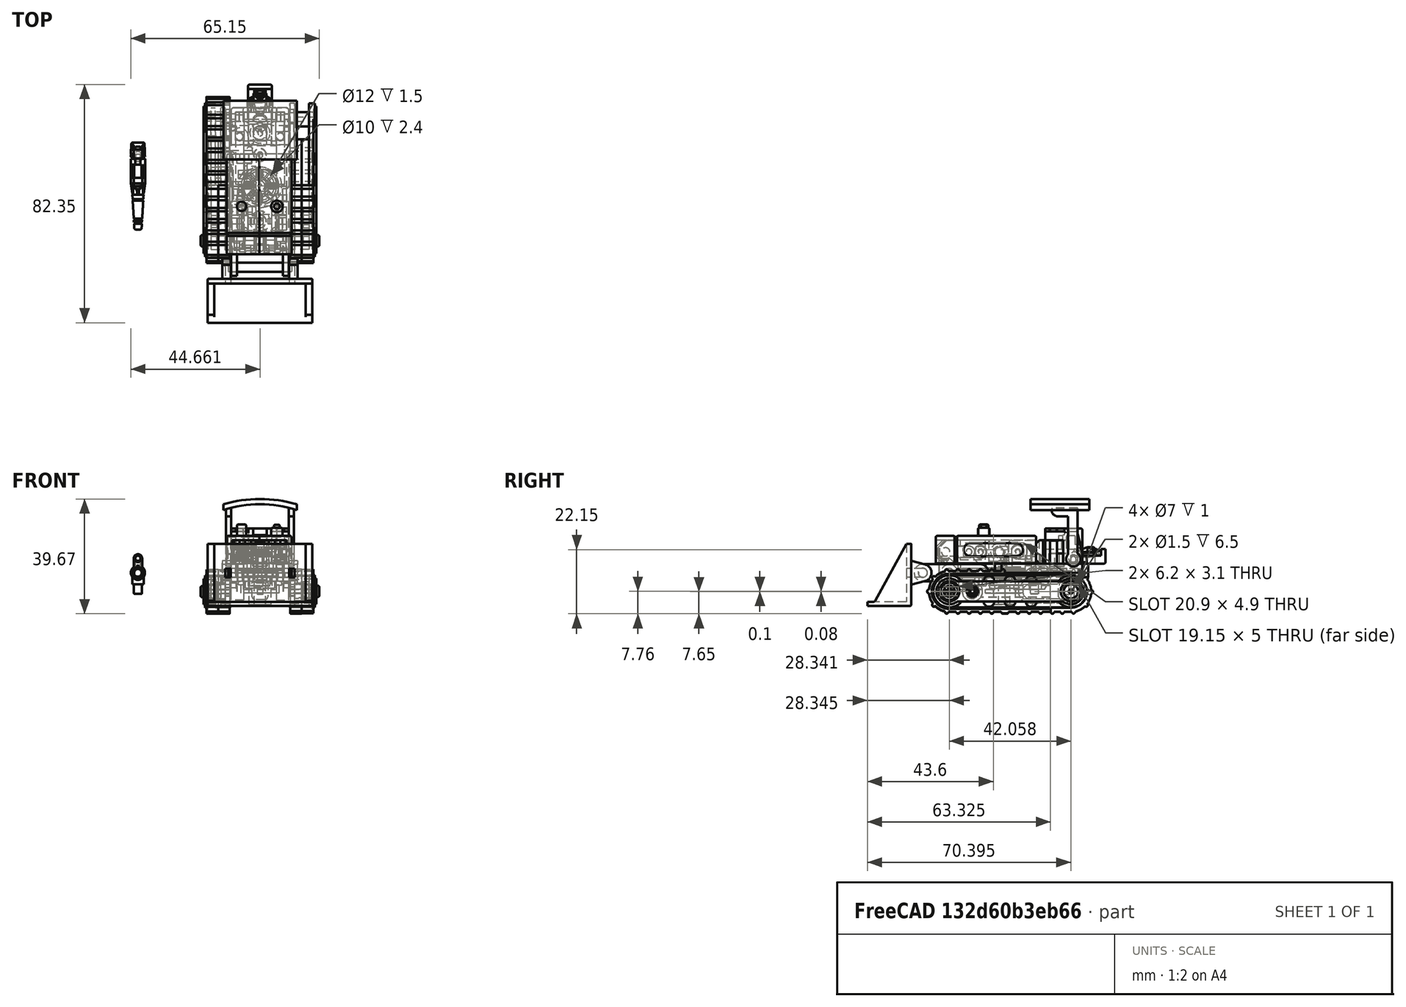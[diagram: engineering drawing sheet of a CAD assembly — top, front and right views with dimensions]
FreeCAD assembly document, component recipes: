
FREECAD ASSEMBLY — COMPONENT RECIPES ("Bonecrusher")

This assembly document has 22 components, labeled P0..P21 below (a component is one placed body or linked part). 22 of them carry a construction recipe — the FreeCAD feature program that regenerates the part from scratch, quoted from this document or its linked companion documents; the rest are supplied as boundary geometry only. No exploded tour is included for this assembly.
NOTE — document 4 of 4 of this assembly tour. The two overview renders and the header above are repeated from document 1; the component sections below continue where the previous document stopped.
COMPONENT P21 — recipe-attached ("Head", modeled in this document).
Construction recipe (the document's own serialized feature program — sketch geometry with constraints, then the solid features built on it; lengths are millimeters unless a unit is written):

FEATURE [Sketcher::SketchObject] Sketch142
  ArcFitTolerance = 1e-06
  AttachmentSupport = -> [XY_Plane015]
  FullyConstrained = true
  MakeInternals = false
  MapMode = 5
  sketch-geometry (4):
    g0: LineSegment StartX=0 StartY=0 StartZ=0 EndX=8.1 EndY=0 EndZ=0
    g1: LineSegment StartX=8.1 StartY=0 StartZ=0 EndX=8.1 EndY=12 EndZ=0
    g2: LineSegment StartX=8.1 StartY=12 StartZ=0 EndX=0 EndY=12 EndZ=0
    g3: LineSegment StartX=0 StartY=12 StartZ=0 EndX=0 EndY=0 EndZ=0
  constraints (11):
    c: Coincident(g0,g1)
    c: Coincident(g1,g2)
    c: Coincident(g2,g3)
    c: Coincident(g3,g0)
    c: Horizontal(g0)
    c: Horizontal(g2)
    c: Vertical(g1)
    c: Vertical(g3)
    c: Coincident(g0,g-1)
    c: DistanceX(g0,g0) = 8.1
    c: DistanceY(g3,g3) = 12
FEATURE [PartDesign::Pad] Pad073
  Direction = (0,0,1)
  Length = 2.8
  Length2 = 10
  Profile = -> Sketch142
  ReferenceAxis = -> Sketch142 [N_Axis]
  Refine = true
  Suppressed = false
  Type = 0
FEATURE [Sketcher::SketchObject] Sketch143
  ArcFitTolerance = 1e-06
  AttachmentSupport = -> [Pad073]
  ExternalGeometry = -> [Pad073]
  FullyConstrained = true
  MakeInternals = false
  MapMode = 5
  Placement = pos=(0,0,2.8) rot=(0,0,1;0rad)
  sketch-geometry (4):
    g0: LineSegment StartX=0 StartY=12 StartZ=0 EndX=0 EndY=10.5 EndZ=0
    g1: LineSegment StartX=0 StartY=10.5 StartZ=0 EndX=8.1 EndY=10.5 EndZ=0
    g2: LineSegment StartX=8.1 StartY=10.5 StartZ=0 EndX=8.1 EndY=12 EndZ=0
    g3: LineSegment StartX=8.1 StartY=12 StartZ=0 EndX=0 EndY=12 EndZ=0
  constraints (11):
    c: Coincident(g0,g1)
    c: Coincident(g1,g2)
    c: Coincident(g2,g3)
    c: Coincident(g3,g0)
    c: Vertical(g0)
    c: Vertical(g2)
    c: Horizontal(g1)
    c: Horizontal(g3)
    c: Coincident(g0,g-4)
    c: PointOnObject(g1,g-3)
    c: DistanceY(g0,g0) = 1.5
FEATURE [PartDesign::Pad] Pad074
  BaseFeature = -> Pad073
  Direction = (0,0,1)
  Length = 2.25
  Length2 = 10
  Profile = -> Sketch143
  ReferenceAxis = -> Sketch143 [N_Axis]
  Refine = true
  Suppressed = false
  Type = 0
FEATURE [Sketcher::SketchObject] Sketch144
  ArcFitTolerance = 1e-06
  AttachmentSupport = -> [Pad074]
  FullyConstrained = true
  MakeInternals = false
  MapMode = 5
  Placement = pos=(0,0,0) rot=(0.57735,-0.57735,-0.57735;2.0944rad)
  sketch-geometry (2):
    g0: ArcOfCircle CenterX=-1.25 CenterY=2.8 CenterZ=0 NormalX=0 NormalY=0 NormalZ=1 AngleXU=0 Radius=1.25 StartAngle=0 EndAngle=3.14159
    g1: LineSegment StartX=-2.5 StartY=2.8 StartZ=0 EndX=-1.29e-14 EndY=2.8 EndZ=0
  constraints (6):
    c: Coincident(g0,g-3)
    c: PointOnObject(g0,g-3)
    c: Diameter(g0) = 2.5
    c: PointOnObject(g0,g-3)
    c: Coincident(g1,g0)
    c: Coincident(g1,g0)
FEATURE [PartDesign::Pad] Pad075
  BaseFeature = -> Pad074
  Direction = (-1,0,0)
  Length = 10
  Length2 = 10
  Profile = -> Sketch144
  ReferenceAxis = -> Sketch144 [N_Axis]
  Refine = true
  Suppressed = false
  Type = 0
FEATURE [Sketcher::SketchObject] Sketch145
  ArcFitTolerance = 1e-06
  AttachmentSupport = -> [Pad075]
  ExternalGeometry = -> [Pad075]
  FullyConstrained = true
  MakeInternals = false
  MapMode = 5
  Placement = pos=(0,0,0) rot=(0.57735,-0.57735,-0.57735;2.0944rad)
  sketch-geometry (2):
    g0: ArcOfCircle CenterX=-1.25 CenterY=2.79999 CenterZ=0 NormalX=0 NormalY=0 NormalZ=1 AngleXU=0 Radius=1.25 StartAngle=7.57041e-06 EndAngle=3.14159
    g1: LineSegment StartX=-2.5 StartY=2.8 StartZ=0 EndX=-3.58256e-11 EndY=2.8 EndZ=0
  constraints (5):
    c: Coincident(g0,g-3)
    c: Coincident(g0,g-3)
    c: Diameter(g0) = 2.5
    c: Coincident(g1,g0)
    c: Coincident(g1,g0)
FEATURE [PartDesign::Pad] Pad076
  BaseFeature = -> Pad075
  Direction = (-1,0,0)
  Length = 9.6
  Length2 = 10
  Profile = -> Sketch145
  ReferenceAxis = -> Sketch145 [N_Axis]
  Refine = true
  Reversed = true
  Suppressed = false
  Type = 0
FEATURE [PartDesign::Pad] Pad077
  BaseFeature = -> Pad076
  Direction = (-1,0,0)
  Length = 1.5
  Length2 = 10
  Profile = -> Sketch145
  ReferenceAxis = -> Sketch145 [N_Axis]
  Refine = true
  Suppressed = false
  Type = 0
FEATURE [Sketcher::SketchObject] Sketch313
  ArcFitTolerance = 1e-06
  AttachmentSupport = -> [Pad077]
  ExternalGeometry = -> [Pad077]
  FullyConstrained = true
  MakeInternals = false
  MapMode = 5
  Placement = pos=(0,0,0) rot=(1,0,0;3.14159rad)
  sketch-geometry (1):
    g0: Circle CenterX=4.05 CenterY=-6 CenterZ=0 NormalX=0 NormalY=0 NormalZ=1 AngleXU=0 Radius=2.35
  constraints (5):
    c: Diameter(g0) = 4.7
    c: DistanceX(g-3,g-3) = 8.1
    c: DistanceY(g-4,g-4) = 12
    c: DistanceY(g0,g-1) = 6
    c: DistanceX(g-1,g0) = 4.05
FEATURE [PartDesign::Pocket] Pocket150
  BaseFeature = -> Pad077
  Direction = (0,0,1)
  Length = 2.2
  Length2 = 5
  Profile = -> Sketch313
  ReferenceAxis = -> Sketch313 [N_Axis]
  Refine = true
  Suppressed = false
  Type = 0
FEATURE [PartDesign::Pad] Pad179
  BaseFeature = -> Pocket150
  Direction = (-1,0,0)
  Length = 0.05
  Length2 = 10
  Profile = -> Pocket150 [Face2]
  Refine = true
  Suppressed = false
  Type = 0
FEATURE [PartDesign::Pad] Pad180
  BaseFeature = -> Pad179
  Direction = (1,0,0)
  Length = 0.05
  Length2 = 10
  Profile = -> Pad179 [Face3]
  Refine = true
  Suppressed = false
  Type = 0
FEATURE [PartDesign::Fillet] Fillet050
  Base = -> Pad180 [Edge7,Edge1,Edge26,Edge21,Edge20]
  BaseFeature = -> Pad180
  Radius = 0.5
  Refine = true
  SupportTransform = false
  Suppressed = false
  UseAllEdges = false
FEATURE [Sketcher::SketchObject] Sketch314
  ArcFitTolerance = 1e-06
  AttachmentOffset = pos=(0,0,-1.9) rot=(0,0,1;0rad)
  AttachmentSupport = -> [Fillet050]
  ExternalGeometry = -> [Fillet050]
  FullyConstrained = true
  MakeInternals = false
  MapMode = 5
  Placement = pos=(1.85,0,0) rot=(0.57735,-0.57735,-0.57735;2.0944rad)
  sketch-geometry (3):
    g0: LineSegment StartX=-5.8 StartY=2.8 StartZ=0 EndX=-9 EndY=2.8 EndZ=0
    g1: LineSegment StartX=-5.8 StartY=2.8 StartZ=0 EndX=-5.8 EndY=5.8 EndZ=0
    g2: ArcOfCircle CenterX=-3.95033 CenterY=0.620354 CenterZ=0 NormalX=0 NormalY=0 NormalZ=1 AngleXU=0 Radius=5.5 StartAngle=1.91379 EndAngle=2.73411
  constraints (10):
    c: PointOnObject(g0,g-3)
    c: PointOnObject(g0,g-3)
    c: DistanceX(g0,g0) = 3.2
    c: DistanceX(g-3,g0) = 1.5
    c: Coincident(g1,g0)
    c: Vertical(g1)
    c: DistanceY(g1,g1) = 3
    c: Coincident(g2,g1)
    c: Coincident(g2,g0)
    c: Radius(g2) = 5.5
FEATURE [PartDesign::Pad] Pad181
  BaseFeature = -> Fillet050
  Direction = (-1,0,0)
  Length = 4.4
  Length2 = 10
  Profile = -> Sketch314
  ReferenceAxis = -> Sketch314 [N_Axis]
  Refine = true
  Reversed = true
  Suppressed = false
  Type = 0
FEATURE [Sketcher::SketchObject] Sketch315
  ArcFitTolerance = 1e-06
  AttachmentSupport = -> [Pad181]
  ExternalGeometry = -> [Pad181]
  FullyConstrained = true
  MakeInternals = false
  MapMode = 5
  Placement = pos=(0,0,2.8) rot=(0,0,1;0rad)
  sketch-geometry (4):
    g0: LineSegment StartX=1.85 StartY=5.8 StartZ=0 EndX=2.7 EndY=2.5 EndZ=0
    g1: LineSegment StartX=6.25 StartY=5.8 StartZ=0 EndX=5.4 EndY=2.5 EndZ=0
    g2: LineSegment StartX=5.4 StartY=2.5 StartZ=0 EndX=2.7 EndY=2.5 EndZ=0
    g3: LineSegment StartX=1.85 StartY=5.8 StartZ=0 EndX=6.25 EndY=5.8 EndZ=0
  constraints (11):
    c: Coincident(g0,g-4)
    c: PointOnObject(g0,g-3)
    c: Coincident(g1,g-4)
    c: PointOnObject(g1,g-3)
    c: Coincident(g2,g1)
    c: Coincident(g2,g0)
    c: DistanceX(g2,g2) = 2.7
    c: DistanceX(g-4,g-4) = 4.4
    c: DistanceX(g0,g0) = 0.85
    c: Coincident(g3,g0)
    c: Coincident(g3,g1)
FEATURE [PartDesign::Pad] Pad182
  BaseFeature = -> Pad181
  Direction = (0,0,1)
  Length = 0.5
  Length2 = 10
  Profile = -> Sketch315
  ReferenceAxis = -> Sketch315 [N_Axis]
  Refine = true
  Suppressed = false
  Type = 0
FEATURE [Sketcher::SketchObject] Sketch316
  ArcFitTolerance = 1e-06
  AttachmentSupport = -> [Pad182]
  ExternalGeometry = -> [Pad182]
  FullyConstrained = true
  MakeInternals = false
  MapMode = 5
  Placement = pos=(0,0,2.8) rot=(0,0,1;0rad)
  sketch-geometry (14):
    g0: LineSegment StartX=2.7 StartY=2.5 StartZ=0 EndX=1.85 EndY=2.5 EndZ=0
    g1: LineSegment StartX=2.7 StartY=2.5 StartZ=0 EndX=1.85 EndY=5.8 EndZ=0
    g2: LineSegment StartX=1.85 StartY=5.8 StartZ=0 EndX=1.55 EndY=5.8 EndZ=0
    g3: LineSegment StartX=1.55 StartY=5.8 StartZ=0 EndX=1.5628 EndY=3.90004 EndZ=0
    g4: LineSegment StartX=1.5628 StartY=3.90004 StartZ=0 EndX=1.85 EndY=3.7 EndZ=0
    g5: LineSegment StartX=1.85 StartY=3.7 StartZ=0 EndX=1.85 EndY=2.5 EndZ=0
    g6: LineSegment StartX=5.4 StartY=2.5 StartZ=0 EndX=6.25 EndY=2.5 EndZ=0
    g7: LineSegment StartX=6.25 StartY=2.5 StartZ=0 EndX=6.25 EndY=3.7 EndZ=0
    g8: LineSegment StartX=6.25 StartY=3.7 StartZ=0 EndX=6.5628 EndY=3.90004 EndZ=0
    g9: LineSegment StartX=6.5628 StartY=3.90004 StartZ=0 EndX=6.55 EndY=5.8 EndZ=0
    g10: LineSegment StartX=6.55 StartY=5.8 StartZ=0 EndX=6.25 EndY=5.8 EndZ=0
    g11: LineSegment StartX=6.25 StartY=5.8 StartZ=0 EndX=5.4 EndY=2.5 EndZ=0
    g12: LineSegment [constr] StartX=1.85 StartY=3.7 StartZ=0 EndX=6.25 EndY=3.7 EndZ=0
    g13: LineSegment [constr] StartX=1.5628 StartY=3.90004 StartZ=0 EndX=6.5628 EndY=3.90004 EndZ=0
  constraints (36):
    c: Coincident(g0,g-4)
    c: Coincident(g1,g0)
    c: Coincident(g1,g-3)
    c: Coincident(g2,g1)
    c: Horizontal(g2)
    c: Coincident(g3,g2)
    c: Coincident(g4,g3)
    c: Coincident(g5,g4)
    c: Coincident(g5,g0)
    c: Vertical(g5)
    c: DistanceY(g5,g5) = 1.2
    c: DistanceX(g-4,g0) = 1.9
    c: DistanceX(g2,g2) = 0.3
    c: PointOnObject(g0,g-4)
    c: Distance(g3) = 1.9
    c: Distance(g4) = 0.35
    c: Coincident(g6,g-6)
    c: PointOnObject(g6,g-6)
    c: Coincident(g7,g6)
    c: Vertical(g7)
    c: Coincident(g8,g7)
    c: Coincident(g9,g8)
    c: Coincident(g10,g9)
    c: Coincident(g10,g-5)
    c: Coincident(g11,g10)
    c: Coincident(g11,g6)
    c: DistanceX(g10,g10) = 0.3
    c: Horizontal(g10)
    c: DistanceX(g6,g-7) = 1.9
    c: Coincident(g12,g4)
    c: Coincident(g12,g7)
    c: Horizontal(g12)
    c: Coincident(g13,g3)
    c: Coincident(g13,g8)
    c: Horizontal(g13)
    c: Distance(g9) = 1.9
FEATURE [PartDesign::Pad] Pad183
  BaseFeature = -> Pad182
  Direction = (0,0,1)
  Length = 0.5
  Length2 = 10
  Profile = -> Sketch316
  ReferenceAxis = -> Sketch316 [N_Axis]
  Refine = true
  Suppressed = false
  Type = 0
FEATURE [Sketcher::SketchObject] Sketch317
  ArcFitTolerance = 1e-06
  AttachmentSupport = -> [Pad183]
  ExternalGeometry = -> [Pad183]
  FullyConstrained = true
  MakeInternals = false
  MapMode = 5
  Placement = pos=(0,0,2.8) rot=(0,0,1;0rad)
  sketch-geometry (20):
    g0: LineSegment StartX=6.5628 StartY=3.90004 StartZ=0 EndX=7.51163 EndY=4.50684 EndZ=0
    g1: LineSegment StartX=7.65 StartY=4.75957 StartZ=0 EndX=7.65 EndY=6.932 EndZ=0
    g2: LineSegment StartX=7.51282 StartY=7.18397 StartZ=0 EndX=6.25 EndY=8 EndZ=0
    g3: LineSegment StartX=6.25 StartY=8 StartZ=0 EndX=6.25 EndY=5.8 EndZ=0
    g4: LineSegment StartX=6.25 StartY=5.8 StartZ=0 EndX=6.55 EndY=5.8 EndZ=0
    g5: LineSegment StartX=6.55 StartY=5.8 StartZ=0 EndX=6.5628 EndY=3.90004 EndZ=0
    g6: ArcOfCircle CenterX=7.35 CenterY=4.75957 CenterZ=0 NormalX=0 NormalY=0 NormalZ=1 AngleXU=0 Radius=0.3 StartAngle=5.28136 EndAngle=6.28319
    g7: GeomPoint [constr] X=7.65 Y=4.59533 Z=0
    g8: ArcOfCircle CenterX=7.35 CenterY=6.932 CenterZ=0 NormalX=0 NormalY=0 NormalZ=1 AngleXU=0 Radius=0.3 StartAngle=1e-16 EndAngle=0.997101
    g9: GeomPoint [constr] X=7.65 Y=7.09533 Z=0
    g10: LineSegment StartX=1.5628 StartY=3.90004 StartZ=0 EndX=1.55 EndY=5.8 EndZ=0
    g11: LineSegment StartX=1.55 StartY=5.8 StartZ=0 EndX=1.85 EndY=5.8 EndZ=0
    g12: LineSegment StartX=1.85 StartY=5.8 StartZ=0 EndX=1.85 EndY=8 EndZ=0
    g13: LineSegment StartX=1.85 StartY=8 StartZ=0 EndX=0.597712 EndY=7.26218 EndZ=0
    g14: LineSegment StartX=1.5628 StartY=3.90004 StartZ=0 EndX=0.578534 EndY=4.58562 EndZ=0
    g15: LineSegment StartX=0.45 StartY=7.0037 StartZ=0 EndX=0.45 EndY=4.83179 EndZ=0
    g16: ArcOfCircle CenterX=0.75 CenterY=7.0037 CenterZ=0 NormalX=0 NormalY=0 NormalZ=1 AngleXU=0 Radius=0.3 StartAngle=2.10322 EndAngle=3.14159
    g17: GeomPoint [constr] X=0.45 Y=7.17515 Z=0
    g18: ArcOfCircle CenterX=0.75 CenterY=4.83179 CenterZ=0 NormalX=0 NormalY=0 NormalZ=1 AngleXU=0 Radius=0.3 StartAngle=3.14159 EndAngle=4.10399
    g19: GeomPoint [constr] X=0.45 Y=4.67515 Z=0
  constraints (46):
    c: Coincident(g0,g-3)
    c: Vertical(g1)
    c: PointOnObject(g2,g-4)
    c: Coincident(g3,g2)
    c: Coincident(g3,g-4)
    c: Coincident(g4,g3)
    c: Coincident(g4,g-3)
    c: Coincident(g5,g4)
    c: Coincident(g5,g0)
    c: DistanceX(g9,g-5) = 0.5
    c: Parallel(g-7,g0)
    c: DistanceY(g7,g9) = 2.5
    c: DistanceY(g3,g3) = 2.2
    c: PointOnObject(g7,g0)
    c: PointOnObject(g7,g1)
    c: Tangent(g0,g6) = -1.5708
    c: Tangent(g1,g6) = -1.5708
    c: PointOnObject(g9,g1)
    c: PointOnObject(g9,g2)
    c: Tangent(g1,g8) = -1.5708
    c: Tangent(g2,g8) = -1.5708
    c: Radius(g8) = 0.3
    c: Radius(g6) = 0.3
    c: Coincident(g10,g-9)
    c: Coincident(g10,g-10)
    c: Coincident(g11,g-9)
    c: Coincident(g11,g-11)
    c: Coincident(g12,g11)
    c: PointOnObject(g12,g-11)
    c: Coincident(g13,g12)
    c: Coincident(g14,g10)
    c: Vertical(g15)
    c: PointOnObject(g17,g13)
    c: PointOnObject(g17,g15)
    c: Tangent(g13,g16) = -1.5708
    c: Tangent(g15,g16) = -1.5708
    c: PointOnObject(g19,g14)
    c: PointOnObject(g19,g15)
    c: Tangent(g14,g18) = 1.5708
    c: Tangent(g15,g18) = -1.5708
    c: Radius(g18) = 0.3
    c: Radius(g16) = 0.3
    c: DistanceX(g-6,g15) = 0.5
    c: DistanceY(g19,g17) = 2.5
    c: DistanceY(g11,g12) = 2.2
    c: Parallel(g-8,g14)
FEATURE [PartDesign::Pad] Pad184
  BaseFeature = -> Pad183
  Direction = (0,0,1)
  Length = 1.2
  Length2 = 10
  Profile = -> Sketch317
  ReferenceAxis = -> Sketch317 [N_Axis]
  Refine = true
  Suppressed = false
  Type = 0
FEATURE [PartDesign::Chamfer] Chamfer003
  Angle = 45
  Base = -> Pad184 [Edge109,Edge61,Edge63,Edge67,Edge65,Edge113,Edge77,Edge79,Edge81,Edge83]
  BaseFeature = -> Pad184
  ChamferType = 0
  FlipDirection = false
  Refine = true
  Size = 0.299
  Size2 = 1
  SupportTransform = false
  Suppressed = false
  UseAllEdges = false
FEATURE [Sketcher::SketchObject] Sketch318
  ArcFitTolerance = 1e-06
  AttachmentSupport = -> [Chamfer003]
  ExternalGeometry = -> [Chamfer003]
  FullyConstrained = true
  MakeInternals = false
  MapMode = 5
  Placement = pos=(0,0,3.3) rot=(0,0,1;0rad)
  sketch-geometry (6):
    g0: LineSegment [constr] StartX=2.7 StartY=2.5 StartZ=0 EndX=1.85 EndY=5.8 EndZ=0
    g1: LineSegment [constr] StartX=5.4 StartY=2.5 StartZ=0 EndX=6.25 EndY=5.8 EndZ=0
    g2: LineSegment StartX=5.91515 StartY=4.5 StartZ=0 EndX=2.18485 EndY=4.5 EndZ=0
    g3: LineSegment StartX=2.18485 StartY=4.5 StartZ=0 EndX=3.02197 EndY=1.25 EndZ=0
    g4: LineSegment StartX=5.91515 StartY=4.5 StartZ=0 EndX=5.07803 EndY=1.25 EndZ=0
    g5: LineSegment StartX=5.07803 StartY=1.25 StartZ=0 EndX=3.02197 EndY=1.25 EndZ=0
  constraints (17):
    c: Coincident(g0,g-3)
    c: Coincident(g0,g-4)
    c: Coincident(g1,g-3)
    c: Coincident(g1,g-4)
    c: PointOnObject(g2,g1)
    c: PointOnObject(g2,g0)
    c: Horizontal(g2)
    c: DistanceY(g0,g2) = 2
    c: Coincident(g3,g2)
    c: Coincident(g4,g2)
    c: Coincident(g5,g4)
    c: Coincident(g5,g3)
    c: Horizontal(g5)
    c: PointOnObject(g0,g3)
    c: PointOnObject(g1,g4)
    c: DistanceY(g-5,g-5) = 2.5
    c: DistanceY(g3,g-5) = 1.25
FEATURE [PartDesign::Pad] Pad185
  BaseFeature = -> Chamfer003
  Direction = (0,0,1)
  Length = 2
  Length2 = 10
  Profile = -> Sketch318
  ReferenceAxis = -> Sketch318 [N_Axis]
  Refine = true
  Suppressed = false
  Type = 0
FEATURE [Sketcher::SketchObject] Sketch319
  ArcFitTolerance = 1e-06
  AttachmentSupport = -> [Pad185]
  ExternalGeometry = -> [Pad185]
  FullyConstrained = true
  MakeInternals = false
  MapMode = 5
  Placement = pos=(1.85,0,0) rot=(0.57735,-0.57735,-0.57735;2.0944rad)
  sketch-geometry (5):
    g0: LineSegment [constr] StartX=-5.8 StartY=5.8 StartZ=0 EndX=-1.25 EndY=4.04999 EndZ=0
    g1: LineSegment StartX=-5.8 StartY=5.8 StartZ=0 EndX=-1.25 EndY=4.04999 EndZ=0
    g2: LineSegment StartX=-1.25 StartY=4.04999 StartZ=0 EndX=-1.25 EndY=5.8 EndZ=0
    g3: LineSegment StartX=-1.25 StartY=5.8 StartZ=0 EndX=-5.8 EndY=5.8 EndZ=0
    g4: LineSegment [constr] StartX=-1.25 StartY=4.04999 StartZ=0 EndX=-1.25 EndY=2.79999 EndZ=0
  constraints (12):
    c: Coincident(g0,g-4)
    c: PointOnObject(g0,g-3)
    c: Coincident(g1,g0)
    c: Coincident(g1,g0)
    c: Coincident(g2,g0)
    c: Coincident(g3,g2)
    c: Coincident(g3,g0)
    c: Horizontal(g3)
    c: Vertical(g2)
    c: Coincident(g4,g0)
    c: Coincident(g4,g-3)
    c: Vertical(g4)
FEATURE [PartDesign::Pocket] Pocket151
  BaseFeature = -> Pad185
  Direction = (1,0,0)
  Length = 5
  Length2 = 5
  Profile = -> Sketch319
  ReferenceAxis = -> Sketch319 [N_Axis]
  Refine = true
  Suppressed = false
  Type = 0
FEATURE [PartDesign::Pad] Pad186
  BaseFeature = -> Pocket151
  Direction = (0,0,1)
  Length = 1
  Length2 = 10
  Profile = -> Sketch318
  ReferenceAxis = -> Sketch318 [N_Axis]
  Refine = true
  Reversed = true
  Suppressed = false
  Type = 0
FEATURE [Sketcher::SketchObject] Sketch320
  ArcFitTolerance = 1e-06
  AttachmentSupport = -> [Pad186]
  ExternalGeometry = -> [Pad186]
  FullyConstrained = true
  MakeInternals = false
  MapMode = 5
  Placement = pos=(1.85,0,0) rot=(0.57735,-0.57735,-0.57735;2.0944rad)
  sketch-geometry (4):
    g0: LineSegment StartX=-3.9 StartY=3.3 StartZ=0 EndX=-2.83669 EndY=4.66026 EndZ=0
    g1: LineSegment StartX=-2.83669 StartY=4.66026 StartZ=0 EndX=-4.5 EndY=5.3 EndZ=0
    g2: LineSegment StartX=-4.5 StartY=5.3 StartZ=0 EndX=-4.5 EndY=3.3 EndZ=0
    g3: LineSegment StartX=-4.5 StartY=3.3 StartZ=0 EndX=-3.9 EndY=3.3 EndZ=0
  constraints (10):
    c: PointOnObject(g0,g-7)
    c: PointOnObject(g0,g-3)
    c: Coincident(g1,g0)
    c: Coincident(g1,g-4)
    c: Coincident(g2,g1)
    c: Coincident(g2,g-7)
    c: Coincident(g3,g2)
    c: Coincident(g3,g0)
    c: Distance(g0,g-3) = 1.7
    c: Distance(g-7,g0) = 1.4
FEATURE [PartDesign::Pocket] Pocket152
  BaseFeature = -> Pad186
  Direction = (1,0,0)
  Length = 5
  Length2 = 5
  Profile = -> Sketch320
  ReferenceAxis = -> Sketch320 [N_Axis]
  Refine = true
  Suppressed = false
  Type = 0
FEATURE [PartDesign::SubShapeBinder] Binder
  BindCopyOnChange = 0
  BindMode = 2
  ClaimChildren = false
  Context = -> Part [Body025.Binder.]
  Fuse = false
  MakeFace = true
  OffsetFill = false
  OffsetIntersection = false
  OffsetJoinType = 0
  OffsetOpenResult = false
  PartialLoad = false
  Refine = true
  Relative = true
  _Version = 2
FEATURE [Sketcher::SketchObject] Sketch321
  ArcFitTolerance = 1e-06
  AttachmentSupport = -> [Binder]
  ExternalGeometry = -> [Binder]
  FullyConstrained = true
  MakeInternals = false
  MapMode = 5
  Placement = pos=(0,0,6.5) rot=(0,0,1;0rad)
  sketch-geometry (6):
    g0: LineSegment StartX=36.1 StartY=-3.2 StartZ=0 EndX=36.85 EndY=-6.15 EndZ=0
    g1: LineSegment StartX=36.85 StartY=-6.15 StartZ=0 EndX=39.55 EndY=-6.15 EndZ=0
    g2: LineSegment StartX=39.55 StartY=-6.15 StartZ=0 EndX=40.3 EndY=-3.2 EndZ=0
    g3: LineSegment StartX=40.3 StartY=-3.2 StartZ=0 EndX=36.1 EndY=-3.2 EndZ=0
    g4: LineSegment [constr] StartX=39.55 StartY=-6.15 StartZ=0 EndX=39.55 EndY=-6.5 EndZ=0
    g5: LineSegment [constr] StartX=36.85 StartY=-6.15 StartZ=0 EndX=36.85 EndY=-6.5 EndZ=0
  constraints (16):
    c: PointOnObject(g0,g-3)
    c: Coincident(g1,g0)
    c: Horizontal(g1)
    c: Coincident(g2,g1)
    c: PointOnObject(g2,g-3)
    c: Coincident(g3,g2)
    c: Coincident(g3,g0)
    c: DistanceX(g-7,g0) = 0.4
    c: DistanceX(g2,g-6) = 0.4
    c: Coincident(g4,g1)
    c: Coincident(g4,g-5)
    c: Vertical(g4)
    c: Coincident(g5,g0)
    c: Coincident(g5,g-8)
    c: Vertical(g5)
    c: DistanceY(g5,g0) = 0.35
FEATURE [PartDesign::Pad] Pad187
  Direction = (0,0,1)
  Length = 2.4
  Length2 = 10
  Profile = -> Sketch321
  ReferenceAxis = -> Sketch321 [N_Axis]
  Refine = true
  Suppressed = false
  Type = 0
FEATURE [PartDesign::SubShapeBinder] Binder002
  BindCopyOnChange = 0
  BindMode = 2
  ClaimChildren = false
  Context = -> Part [Body025.Binder002.]
  Fuse = false
  MakeFace = true
  OffsetFill = false
  OffsetIntersection = false
  OffsetJoinType = 0
  OffsetOpenResult = false
  PartialLoad = false
  Refine = true
  Relative = true
  _Version = 2
FEATURE [Sketcher::SketchObject] Sketch322
  ArcFitTolerance = 1e-06
  AttachmentSupport = -> [Binder002]
  ExternalGeometry = -> [Pad187]
  FullyConstrained = true
  MakeInternals = false
  MapMode = 5
  Placement = pos=(36,0,0) rot=(0.57735,-0.57735,-0.57735;2.0944rad)
  sketch-geometry (3):
    g0: LineSegment StartX=6.15 StartY=7.8 StartZ=0 EndX=3.2 EndY=8.9 EndZ=0
    g1: LineSegment StartX=3.2 StartY=8.9 StartZ=0 EndX=6.15 EndY=8.9 EndZ=0
    g2: LineSegment StartX=6.15 StartY=8.9 StartZ=0 EndX=6.15 EndY=7.8 EndZ=0
  constraints (7):
    c: PointOnObject(g0,g-4)
    c: Coincident(g0,g-3)
    c: Coincident(g1,g0)
    c: Coincident(g1,g-4)
    c: Coincident(g2,g1)
    c: Coincident(g2,g0)
    c: DistanceY(g2,g2) = 1.1
FEATURE [PartDesign::Pocket] Pocket153
  BaseFeature = -> Pad187
  Direction = (1,0,0)
  Length = 5
  Length2 = 5
  Profile = -> Sketch322
  ReferenceAxis = -> Sketch322 [N_Axis]
  Refine = true
  Suppressed = false
  Type = 0
FEATURE [Sketcher::SketchObject] Sketch323
  ArcFitTolerance = 1e-06
  AttachmentSupport = -> [Binder002]
  ExternalGeometry = -> [Pocket153]
  FullyConstrained = true
  MakeInternals = false
  MapMode = 5
  Placement = pos=(36,0,0) rot=(0.57735,-0.57735,-0.57735;2.0944rad)
  sketch-geometry (4):
    g0: LineSegment StartX=6.12376 StartY=7.80978 StartZ=0 EndX=5.1 EndY=6.5 EndZ=0
    g1: LineSegment StartX=5.1 StartY=6.5 StartZ=0 EndX=6.15 EndY=6.5 EndZ=0
    g2: LineSegment StartX=6.15 StartY=6.5 StartZ=0 EndX=6.15 EndY=7.8 EndZ=0
    g3: LineSegment StartX=6.15 StartY=7.8 StartZ=0 EndX=6.12376 EndY=7.80978 EndZ=0
  constraints (10):
    c: PointOnObject(g0,g-3)
    c: PointOnObject(g0,g-5)
    c: Coincident(g1,g0)
    c: Coincident(g1,g-5)
    c: Coincident(g2,g1)
    c: Coincident(g2,g-4)
    c: Coincident(g3,g2)
    c: Coincident(g3,g0)
    c: DistanceX(g1,g1) = 1.05
    c: Distance(g3) = 0.028
FEATURE [PartDesign::Pocket] Pocket154
  BaseFeature = -> Pocket153
  Direction = (1,0,0)
  Length = 5
  Length2 = 5
  Profile = -> Sketch323
  ReferenceAxis = -> Sketch323 [N_Axis]
  Refine = true
  Suppressed = false
  Type = 0
FEATURE [PartDesign::Body] Body025  label="Visor"
  AllowCompound = false
  Group = -> [Binder,Sketch321,Pad187,Binder002,Sketch322,Pocket153,Sketch323,Pocket154]
  Origin = -> Origin028
  Tip = -> Pocket154
FEATURE [Sketcher::SketchObject] Sketch324
  ArcFitTolerance = 1e-06
  AttachmentOffset = pos=(0,0,-2.2) rot=(0,0,1;0rad)
  AttachmentSupport = -> [Pocket152]
  ExternalGeometry = -> [Pocket152]
  FullyConstrained = true
  MakeInternals = false
  MapMode = 5
  Placement = pos=(0,2.2,-2.09833e-11) rot=(1,0,0;1.5708rad)
  sketch-geometry (4):
    g0: LineSegment StartX=3.34997 StartY=4.04999 StartZ=0 EndX=4.74997 EndY=4.04999 EndZ=0
    g1: LineSegment StartX=4.74997 StartY=4.04999 StartZ=0 EndX=4.74997 EndY=5.04999 EndZ=0
    g2: LineSegment StartX=4.74997 StartY=5.04999 StartZ=0 EndX=3.34997 EndY=5.04999 EndZ=0
    g3: LineSegment StartX=3.34997 StartY=5.04999 StartZ=0 EndX=3.34997 EndY=4.04999 EndZ=0
  constraints (13):
    c: Coincident(g0,g1)
    c: Coincident(g1,g2)
    c: Coincident(g2,g3)
    c: Coincident(g3,g0)
    c: Horizontal(g0)
    c: Horizontal(g2)
    c: Vertical(g1)
    c: Vertical(g3)
    c: PointOnObject(g0,g-3)
    c: DistanceX(g2,g2) = 1.4
    c: DistanceX(g-3,g-3) = 2.05606
    c: DistanceX(g-3,g0) = 0.328
    c: DistanceY(g3,g3) = 1
FEATURE [PartDesign::Pad] Pad188
  BaseFeature = -> Pocket152
  Direction = (0,-1,9.5379e-12)
  Length = 0.95
  Length2 = 10
  Profile = -> Sketch324
  ReferenceAxis = -> Sketch324 [N_Axis]
  Refine = true
  Suppressed = false
  Type = 0
FEATURE [Sketcher::SketchObject] Sketch325
  ArcFitTolerance = 1e-06
  AttachmentSupport = -> [Pad188]
  ExternalGeometry = -> [Pad188]
  FullyConstrained = true
  MakeInternals = false
  MapMode = 5
  Placement = pos=(3.34997,0,0) rot=(0.57735,-0.57735,-0.57735;2.0944rad)
  sketch-geometry (3):
    g0: LineSegment StartX=-1.75 StartY=5.04999 StartZ=0 EndX=-2.2 EndY=5.04999 EndZ=0
    g1: LineSegment StartX=-2.2 StartY=5.04999 StartZ=0 EndX=-2.2 EndY=4.41538 EndZ=0
    g2: LineSegment StartX=-2.2 StartY=4.41538 StartZ=0 EndX=-1.75 EndY=5.04999 EndZ=0
  constraints (7):
    c: Coincident(g0,g-5)
    c: Horizontal(g0)
    c: Coincident(g1,g0)
    c: Coincident(g1,g-5)
    c: Coincident(g2,g1)
    c: Coincident(g2,g0)
    c: DistanceX(g0,g-4) = 0.5
FEATURE [PartDesign::Pocket] Pocket155
  BaseFeature = -> Pad188
  Direction = (1,0,0)
  Length = 5
  Length2 = 5
  Profile = -> Sketch325
  ReferenceAxis = -> Sketch325 [N_Axis]
  Refine = true
  Suppressed = false
  Type = 0
FEATURE [Sketcher::SketchObject] Sketch326
  ArcFitTolerance = 1e-06
  AttachmentOffset = pos=(0,0,-0.7) rot=(0,0,1;0rad)
  AttachmentSupport = -> [Pocket155]
  ExternalGeometry = -> [Pocket155]
  FullyConstrained = true
  MakeInternals = false
  MapMode = 5
  Placement = pos=(0,0,4.35) rot=(0,0,1;0rad)
  sketch-geometry (8):
    g0: LineSegment StartX=2.05 StartY=10.5 StartZ=0 EndX=2.05 EndY=7.5 EndZ=0
    g1: LineSegment StartX=2.05 StartY=7.5 StartZ=0 EndX=2.65 EndY=7.5 EndZ=0
    g2: LineSegment StartX=2.65 StartY=7.5 StartZ=0 EndX=2.65 EndY=10.5 EndZ=0
    g3: LineSegment StartX=2.65 StartY=10.5 StartZ=0 EndX=2.05 EndY=10.5 EndZ=0
    g4: LineSegment StartX=5.45 StartY=10.5 StartZ=0 EndX=5.45 EndY=7.5 EndZ=0
    g5: LineSegment StartX=5.45 StartY=7.5 StartZ=0 EndX=6.05 EndY=7.5 EndZ=0
    g6: LineSegment StartX=6.05 StartY=7.5 StartZ=0 EndX=6.05 EndY=10.5 EndZ=0
    g7: LineSegment StartX=6.05 StartY=10.5 StartZ=0 EndX=5.45 EndY=10.5 EndZ=0
  constraints (24):
    c: Coincident(g0,g1)
    c: Coincident(g1,g2)
    c: Coincident(g2,g3)
    c: Coincident(g3,g0)
    c: Vertical(g0)
    c: Vertical(g2)
    c: Horizontal(g1)
    c: Horizontal(g3)
    c: PointOnObject(g0,g-3)
    c: Coincident(g4,g5)
    c: Coincident(g5,g6)
    c: Coincident(g6,g7)
    c: Coincident(g7,g4)
    c: Vertical(g4)
    c: Vertical(g6)
    c: Horizontal(g5)
    c: Horizontal(g7)
    c: PointOnObject(g4,g-3)
    c: DistanceX(g1,g1) = 0.6
    c: DistanceX(g7,g7) = 0.6
    c: DistanceX(g6,g-4) = 0.2
    c: DistanceX(g-4,g0) = 0.2
    c: DistanceY(g0,g0) = 3
    c: DistanceY(g4,g4) = 3
FEATURE [PartDesign::Pad] Pad189
  BaseFeature = -> Pocket155
  Direction = (0,0,1)
  Length = 2
  Length2 = 10
  Profile = -> Sketch326
  ReferenceAxis = -> Sketch326 [N_Axis]
  Refine = true
  Reversed = true
  Suppressed = false
  Type = 0
FEATURE [Sketcher::SketchObject] Sketch327
  ArcFitTolerance = 1e-06
  AttachmentSupport = -> [Pad189]
  ExternalGeometry = -> [Pad189]
  FullyConstrained = true
  MakeInternals = false
  MapMode = 5
  Placement = pos=(0,0,5.05) rot=(0,0,1;0rad)
  sketch-geometry (4):
    g0: LineSegment StartX=3.2 StartY=10 StartZ=0 EndX=4.9 EndY=10 EndZ=0
    g1: LineSegment StartX=4.9 StartY=10 StartZ=0 EndX=5.15 EndY=7.2 EndZ=0
    g2: LineSegment StartX=5.15 StartY=7.2 StartZ=0 EndX=2.95 EndY=7.2 EndZ=0
    g3: LineSegment StartX=3.2 StartY=10 StartZ=0 EndX=2.95 EndY=7.2 EndZ=0
  constraints (13):
    c: Horizontal(g0)
    c: Coincident(g1,g0)
    c: Coincident(g2,g1)
    c: Horizontal(g2)
    c: Coincident(g3,g0)
    c: Coincident(g3,g2)
    c: DistanceY(g0,g-3) = 0.5
    c: DistanceX(g0,g0) = 1.7
    c: DistanceX(g2,g2) = 2.2
    c: DistanceX(g2,g0) = 0.25
    c: DistanceY(g2,g0) = 2.8
    c: DistanceX(g-4,g-5) = 2.8
    c: DistanceX(g-4,g0) = 0.55
FEATURE [PartDesign::Pad] Pad190
  BaseFeature = -> Pad189
  Direction = (0,0,1)
  Length = 2.3
  Length2 = 10
  Profile = -> Sketch327
  ReferenceAxis = -> Sketch327 [N_Axis]
  Refine = true
  Reversed = true
  Suppressed = false
  Type = 0
FEATURE [Sketcher::SketchObject] Sketch328
  ArcFitTolerance = 1e-06
  AttachmentOffset = pos=(0,0,-1) rot=(0,0,1;0rad)
  AttachmentSupport = -> [Pad190]
  ExternalGeometry = -> [Pad190]
  FullyConstrained = true
  MakeInternals = false
  MapMode = 5
  Placement = pos=(3.05,0,0) rot=(0.57735,-0.57735,-0.57735;2.0944rad)
  sketch-geometry (4):
    g0: LineSegment StartX=-10 StartY=2.8 StartZ=0 EndX=-9 EndY=5.05 EndZ=0
    g1: LineSegment StartX=-9 StartY=5.05 StartZ=0 EndX=-10 EndY=5.05 EndZ=0
    g2: LineSegment StartX=-10 StartY=5.05 StartZ=0 EndX=-10 EndY=2.8 EndZ=0
    g3: LineSegment [constr] StartX=-9 StartY=5.05 StartZ=0 EndX=-9 EndY=2.8 EndZ=0
  constraints (9):
    c: Coincident(g0,g-4)
    c: PointOnObject(g0,g-3)
    c: Coincident(g1,g0)
    c: Coincident(g1,g-4)
    c: Coincident(g2,g1)
    c: Coincident(g2,g0)
    c: Coincident(g3,g0)
    c: Coincident(g3,g-5)
    c: Vertical(g3)
FEATURE [PartDesign::Pocket] Pocket156
  BaseFeature = -> Pad190
  Direction = (1,0,0)
  Length = 2
  Length2 = 5
  Profile = -> Sketch328
  ReferenceAxis = -> Sketch328 [N_Axis]
  Refine = true
  Suppressed = false
  Type = 0
FEATURE [Sketcher::SketchObject] Sketch329
  ArcFitTolerance = 1e-06
  AttachmentSupport = -> [Pocket156]
  ExternalGeometry = -> [Pocket156]
  FullyConstrained = true
  MakeInternals = false
  MapMode = 5
  Placement = pos=(0,0,5.05) rot=(0,0,1;0rad)
  sketch-geometry (4):
    g0: LineSegment StartX=3.55093 StartY=8.5 StartZ=0 EndX=3.55093 EndY=6.1 EndZ=0
    g1: LineSegment StartX=3.55093 StartY=6.1 StartZ=0 EndX=4.54907 EndY=6.1 EndZ=0
    g2: LineSegment StartX=4.54907 StartY=6.1 StartZ=0 EndX=4.54907 EndY=8.5 EndZ=0
    g3: LineSegment StartX=4.54907 StartY=8.5 StartZ=0 EndX=3.55093 EndY=8.5 EndZ=0
  constraints (13):
    c: Coincident(g0,g1)
    c: Coincident(g1,g2)
    c: Coincident(g2,g3)
    c: Coincident(g3,g0)
    c: Vertical(g0)
    c: Vertical(g2)
    c: Horizontal(g1)
    c: Horizontal(g3)
    c: DistanceX(g-4,g-5) = 2.19814
    c: DistanceX(g-4,g0) = 0.6
    c: DistanceX(g2,g-5) = 0.6
    c: DistanceY(g0,g0) = 2.4
    c: DistanceY(g0,g-3) = 1.5
FEATURE [PartDesign::Pad] Pad191
  BaseFeature = -> Pocket156
  Direction = (0,0,1)
  Length = 0.6
  Length2 = 10
  Profile = -> Sketch329
  ReferenceAxis = -> Sketch329 [N_Axis]
  Refine = true
  Suppressed = false
  Type = 0
FEATURE [Sketcher::SketchObject] Sketch330
  ArcFitTolerance = 1e-06
  AttachmentSupport = -> [Pad191]
  ExternalGeometry = -> [Pad191]
  FullyConstrained = true
  MakeInternals = false
  MapMode = 5
  Placement = pos=(3.55093,0,0) rot=(0.57735,-0.57735,-0.57735;2.0944rad)
  sketch-geometry (3):
    g0: LineSegment StartX=-8.5 StartY=5.05 StartZ=0 EndX=-8.5 EndY=5.65 EndZ=0
    g1: LineSegment StartX=-8.5 StartY=5.65 StartZ=0 EndX=-8 EndY=5.65 EndZ=0
    g2: LineSegment StartX=-8 StartY=5.65 StartZ=0 EndX=-8.5 EndY=5.05 EndZ=0
  constraints (7):
    c: Coincident(g0,g-4)
    c: Coincident(g0,g-4)
    c: Coincident(g1,g0)
    c: PointOnObject(g1,g-3)
    c: Coincident(g2,g1)
    c: Coincident(g2,g0)
    c: DistanceX(g1,g1) = 0.5
FEATURE [PartDesign::Pocket] Pocket157
  BaseFeature = -> Pad191
  Direction = (1,0,0)
  Length = 5
  Length2 = 5
  Profile = -> Sketch330
  ReferenceAxis = -> Sketch330 [N_Axis]
  Refine = true
  Suppressed = false
  Type = 0
FEATURE [Sketcher::SketchObject] Sketch335
  ArcFitTolerance = 1e-06
  AttachmentSupport = -> [Pocket157]
  ExternalGeometry = -> [Pocket157]
  FullyConstrained = true
  MakeInternals = false
  MapMode = 5
  Placement = pos=(-0.05,0,0) rot=(0.57735,-0.57735,-0.57735;2.0944rad)
  sketch-geometry (4):
    g0: LineSegment StartX=0 StartY=2.8 StartZ=0 EndX=-5.5 EndY=2.8 EndZ=0
    g1: LineSegment StartX=-5.5 StartY=2.8 StartZ=0 EndX=-5.5 EndY=0.5 EndZ=0
    g2: LineSegment StartX=-5.5 StartY=0.5 StartZ=0 EndX=0 EndY=0.5 EndZ=0
    g3: LineSegment StartX=0 StartY=0.5 StartZ=0 EndX=0 EndY=2.8 EndZ=0
  constraints (12):
    c: Coincident(g0,g1)
    c: Coincident(g1,g2)
    c: Coincident(g2,g3)
    c: Coincident(g3,g0)
    c: Horizontal(g0)
    c: Horizontal(g2)
    c: Vertical(g1)
    c: Vertical(g3)
    c: PointOnObject(g0,g-3)
    c: PointOnObject(g1,g-6)
    c: DistanceX(g2,g2) = 5.5
    c: PointOnObject(g0,g-5)
FEATURE [PartDesign::Body] Body013  label="Main_Head"
  AllowCompound = false
  Group = -> [Sketch142,Pad073,Sketch143,Pad074,Sketch144,Pad075,Sketch145,Pad076,Pad077,Sketch313,Pocket150,Pad179,Pad180,Fillet050,Sketch314,Pad181,Sketch315,Pad182,Sketch316,Pad183,Sketch317,Pad184,Chamfer003,Sketch318,Pad185,Sketch319,Pocket151,Pad186,Sketch320,Pocket152,Sketch324,Pad188,Sketch325,Pocket155,Sketch326,Pad189,Sketch327,Pad190,Sketch328,Pocket156,Sketch329,Pad191,Sketch330,Pocket157,Sketch335,+3 more]
  Origin = -> Origin015
  Placement = pos=(34.15,-9,3.2) rot=(0,0,1;0rad)
  Tip = -> Pad200
PROVENANCE & LICENSES
A FreeCAD (.FCStd) document from a public repository crawl; recipes are the document's own serialized feature recipes (and, for linked parts, companion documents' recipes).
License: as declared in the source repository (recorded in the dataset sidecar).
